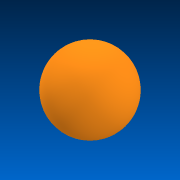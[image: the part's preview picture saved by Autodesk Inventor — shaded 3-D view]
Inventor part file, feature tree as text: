
AUTODESK INVENTOR PART (.ipt)
format: ipt  version: 2022.2 (Build 262287000, 287)  size: 102,912 bytes
history: native  units: in
note: dims shown in document units (in); Inventor stores cm internally (conversion verified against a paired STEP export)
features: revolve x1, sketch x1
ambient origin geometry x8: Origin, YZ Plane, XZ Plane, XY Plane, X Axis, Y Axis, Z Axis, Center Point
bodies: Solid1 (feature_tree)
feature tree (2):
  revolve  "Revolution1"  Angle=180.0deg
  sketch  "Sketch1"  dims[d0=9.3901in d1=180.0deg]
